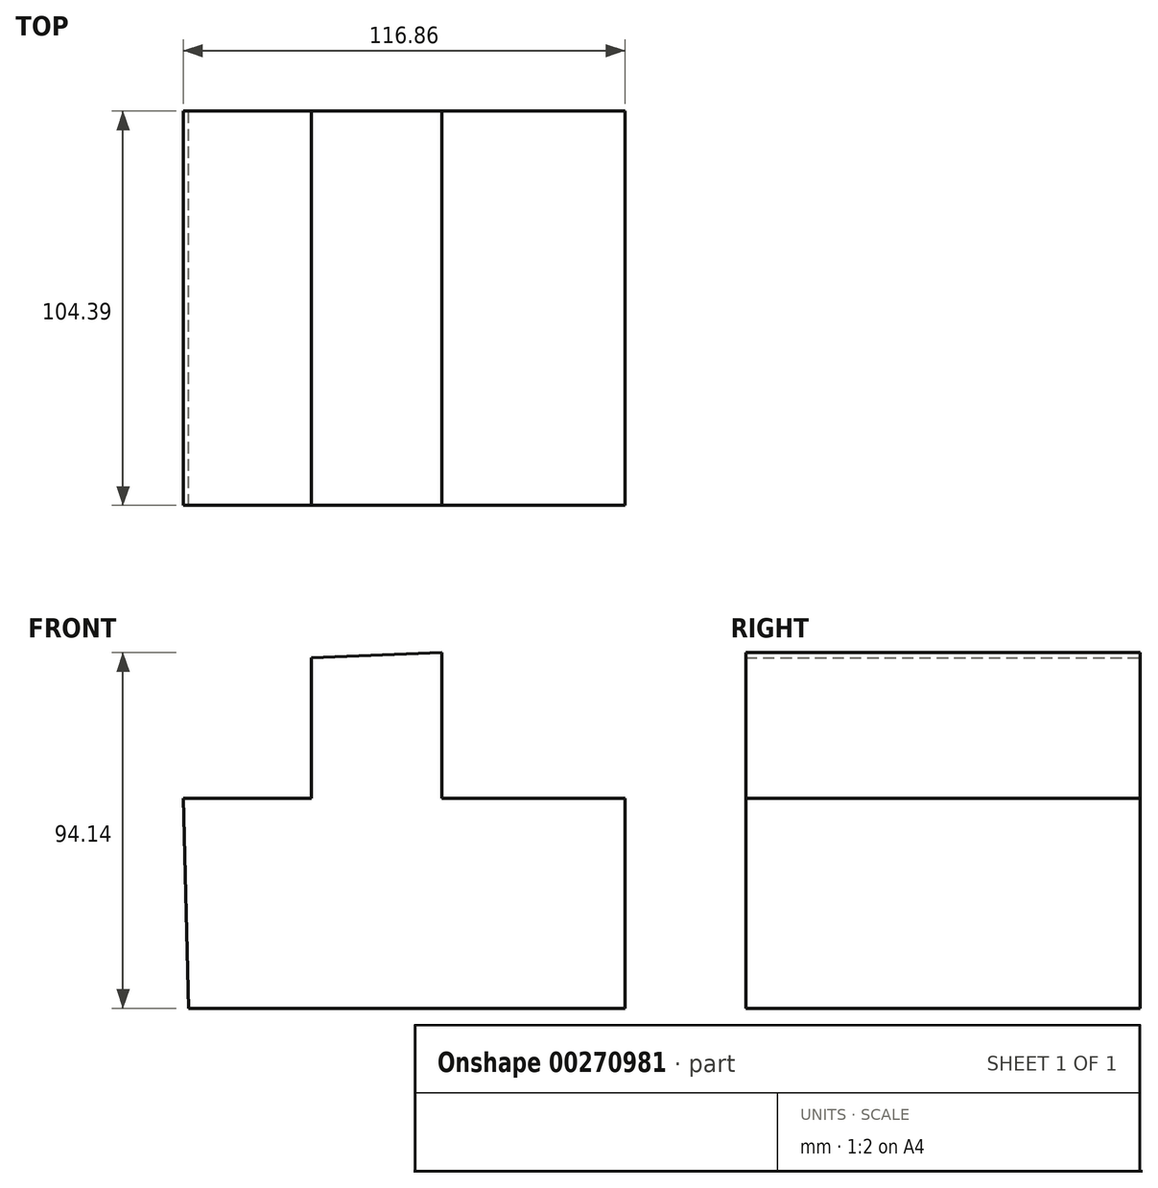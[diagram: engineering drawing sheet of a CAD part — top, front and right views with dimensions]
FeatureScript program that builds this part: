
annotation { "Feature Type Name" : "Feature", "Feature Type Description" : "" }
export const myFeature = defineFeature(function(context is Context, id is Id, definition is map)
    precondition{}
    {
        {
            var Q0;
            Q0=qCreatedBy(makeId("Front.planeOp"),FACE);
            var sketch = newSketch(context, id + "F0", { "sketchPlane" : qUnion([Q0])});
            skLineSegment(sketch, "E0", {"start": v(-28.17, 37.24) * mm, "end": v(-28.17, 0) * mm});
            skLineSegment(sketch, "E1", {"start": v(-28.17, 0) * mm, "end": v(-61.96, 0) * mm});
            skLineSegment(sketch, "E2", {"start": v(-61.96, 0) * mm, "end": v(-60.63, -55.57) * mm});
            skLineSegment(sketch, "E3", {"start": v(-60.63, -55.57) * mm, "end": v(-15.56, -55.57) * mm});
            skLineSegment(sketch, "E4", {"start": v(-15.56, -55.57) * mm, "end": v(54.9, -55.57) * mm});
            skLineSegment(sketch, "E5", {"start": v(54.9, -55.57) * mm, "end": v(54.9, 0) * mm});
            skLineSegment(sketch, "E6", {"start": v(54.9, 0) * mm, "end": v(6.4, 0) * mm});
            skLineSegment(sketch, "E7", {"start": v(6.4, 0) * mm, "end": v(6.4, 38.57) * mm});
            skLineSegment(sketch, "E8", {"start": v(6.4, 38.57) * mm, "end": v(-28.17, 37.24) * mm});
            skSolve(sketch);
        }
        {
            var Q0;
            Q0 = qSketchRegion(id + "F0", true);
            extrude(context, id + "F1", {"entities" : qUnion([Q0]), "depth" : 104.4 * mm});
        }
    });
